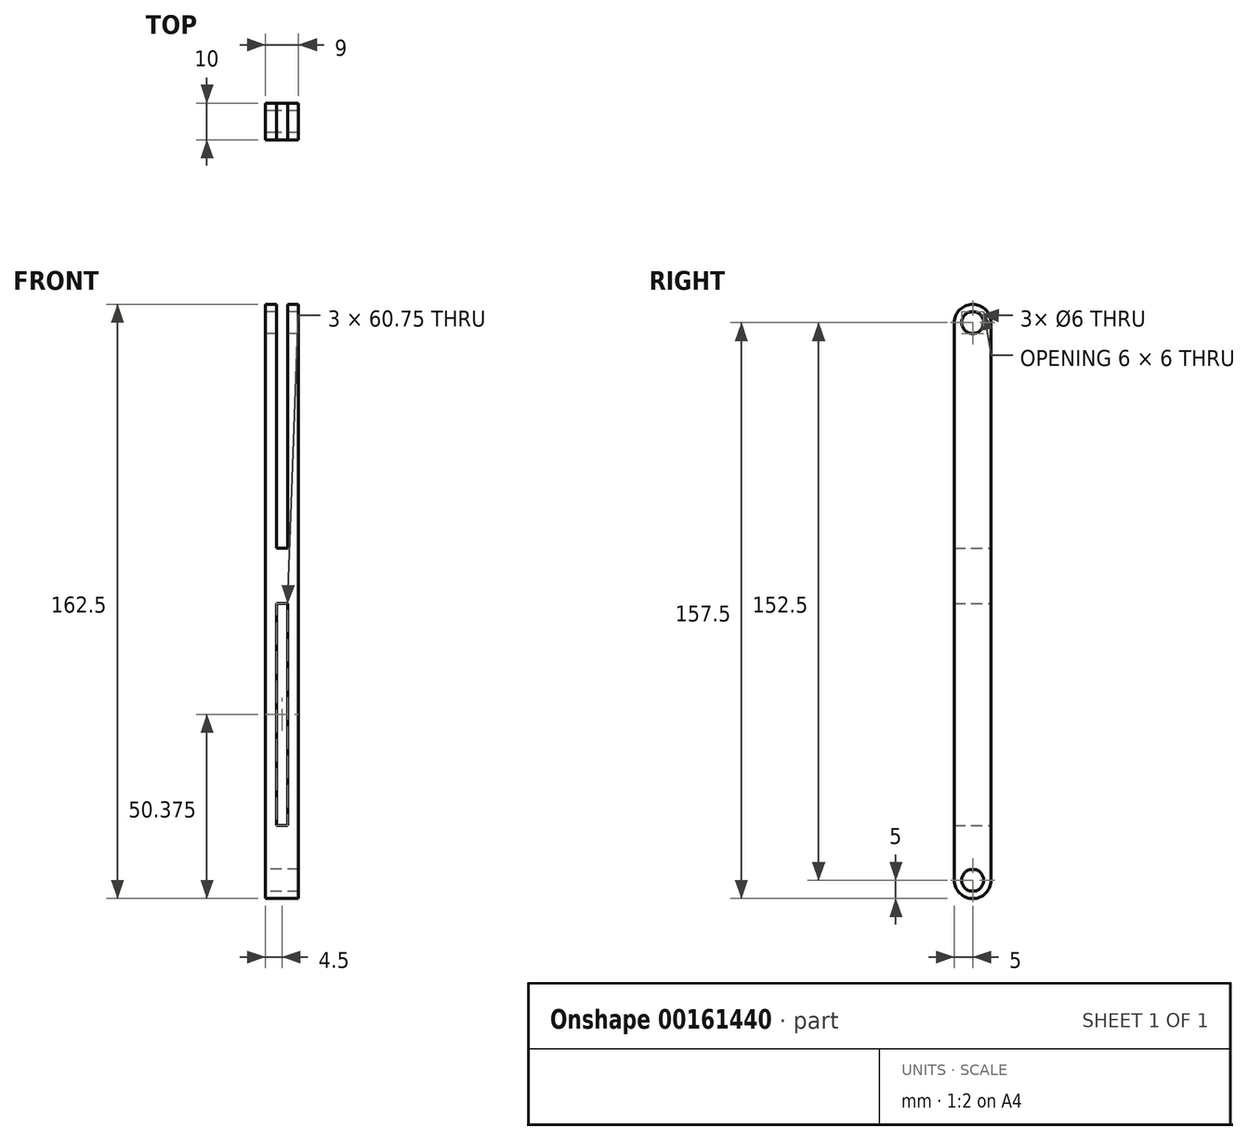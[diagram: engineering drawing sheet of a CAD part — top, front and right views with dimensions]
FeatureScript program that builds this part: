
annotation { "Feature Type Name" : "Feature", "Feature Type Description" : "" }
export const myFeature = defineFeature(function(context is Context, id is Id, definition is map)
    precondition{}
    {
        {
            var Q0;
            Q0=qCreatedBy(makeId("Right.planeOp"),FACE);
            var sketch = newSketch(context, id + "F0", { "sketchPlane" : qUnion([Q0])});
            skLineSegment(sketch, "E0.left", {"start": v(5, 76.25) * mm, "end": v(5, -76.25) * mm});
            skLineSegment(sketch, "E0.right", {"start": v(-5, 76.25) * mm, "end": v(-5, -76.25) * mm});
            skPoint(sketch, "E0.middle", {"position": v(0, 0) * mm});
            skArc(sketch, "E1", {"start": v(5, 76.25) * mm, "mid": v(0, 81.25) * mm, "end": v(-5, 76.25) * mm});
            skArc(sketch, "E2", {"start": v(-5, -76.25) * mm, "mid": v(0, -81.25) * mm, "end": v(5, -76.25) * mm});
            skCircle(sketch, "E3", {"center": v(0, 76.25) * mm, "radius": 3 * mm});
            skCircle(sketch, "E4", {"center": v(0, -76.25) * mm, "radius": 3 * mm});
            skSolve(sketch);
        }
        {
            var Q0;
            Q0=makeQuery(id+"F0.imprint","IMPRINT",FACE,{"disambiguationData":[TD([[makeQuery(id+"F0.imprint","IMPRINT",EDGE,{"derivedFrom":sQuery(id+"F0.wireOp",EDGE,"E0.left")}),-1.0]])]});
            extrude(context, id + "F1", {"entities" : qUnion([Q0]), "depth" : 9 * mm});
        }
        {
            var Q0;
            Q0=makeQuery(id+"F1.opExtrude","SWEPT_FACE",FACE,{"disambiguationData":[OSD([sQuery(id+"F0.wireOp",EDGE,"E0.left")])]});
            var sketch = newSketch(context, id + "F2", { "sketchPlane" : qUnion([Q0])});
            skLineSegment(sketch, "E5.bottom", {"start": v(-6, -61.25) * mm, "end": v(-3, -61.25) * mm});
            skLineSegment(sketch, "E5.top", {"start": v(-6, 81.25) * mm, "end": v(-3, 81.25) * mm});
            skLineSegment(sketch, "E5.left", {"start": v(-6, -61.25) * mm, "end": v(-6, -0.5) * mm});
            skLineSegment(sketch, "E5.right", {"start": v(-3, -61.25) * mm, "end": v(-3, -0.5) * mm});
            skLineSegment(sketch, "E6", {"start": v(-6, 14.5) * mm, "end": v(-3, 14.5) * mm});
            skLineSegment(sketch, "E7", {"start": v(-6, -0.5) * mm, "end": v(-3, -0.5) * mm});
            skPoint(sketch, "E8", {"position": v(-6, 10) * mm});
            skPoint(sketch, "E9", {"position": v(-3, 10) * mm});
            skPoint(sketch, "E10", {"position": v(-3, 14.5) * mm});
            skPoint(sketch, "E11", {"position": v(-6, 14.5) * mm});
            skPoint(sketch, "E12", {"position": v(-6, -0.5) * mm});
            skPoint(sketch, "E13", {"position": v(-3, -0.5) * mm});
            skLineSegment(sketch, "E14.trimOffspring", {"start": v(-3, 14.5) * mm, "end": v(-3, 81.25) * mm});
            skLineSegment(sketch, "E15.trimOffspring", {"start": v(-6, 14.5) * mm, "end": v(-6, 81.25) * mm});
            skSolve(sketch);
        }
        {
            var Q0;
            {var subQ0=sQuery(id+"F2.wireOp",EDGE,"E6");Q0=makeQuery(id+"F2.imprint","IMPRINT",FACE,{"disambiguationData":[TD([[makeQuery(id+"F2.imprint","IMPRINT",EDGE,{"derivedFrom":subQ0}),1.0]])]});}
            var Q1;
            {var subQ0=sQuery(id+"F2.wireOp",EDGE,"E5.top");Q1=makeQuery(id+"F2.imprint","IMPRINT",FACE,{"disambiguationData":[TD([[makeQuery(id+"F2.imprint","IMPRINT",EDGE,{"derivedFrom":subQ0}),-1.0]])]});}
            var Q2;
            Q2=makeQuery(id+"F2.imprint","IMPRINT",FACE,{"disambiguationData":[TD([[makeQuery(id+"F2.imprint","IMPRINT",EDGE,{"derivedFrom":sQuery(id+"F2.wireOp",EDGE,"E5.bottom")}),1.0]])]});
            extrude(context, id + "F3", {"entities" : qUnion([Q0, Q1, Q2]), "operationType" : NewBodyOperationType.REMOVE, "oppositeDirection" : true, "depth" : 10 * mm});
        }
    });
